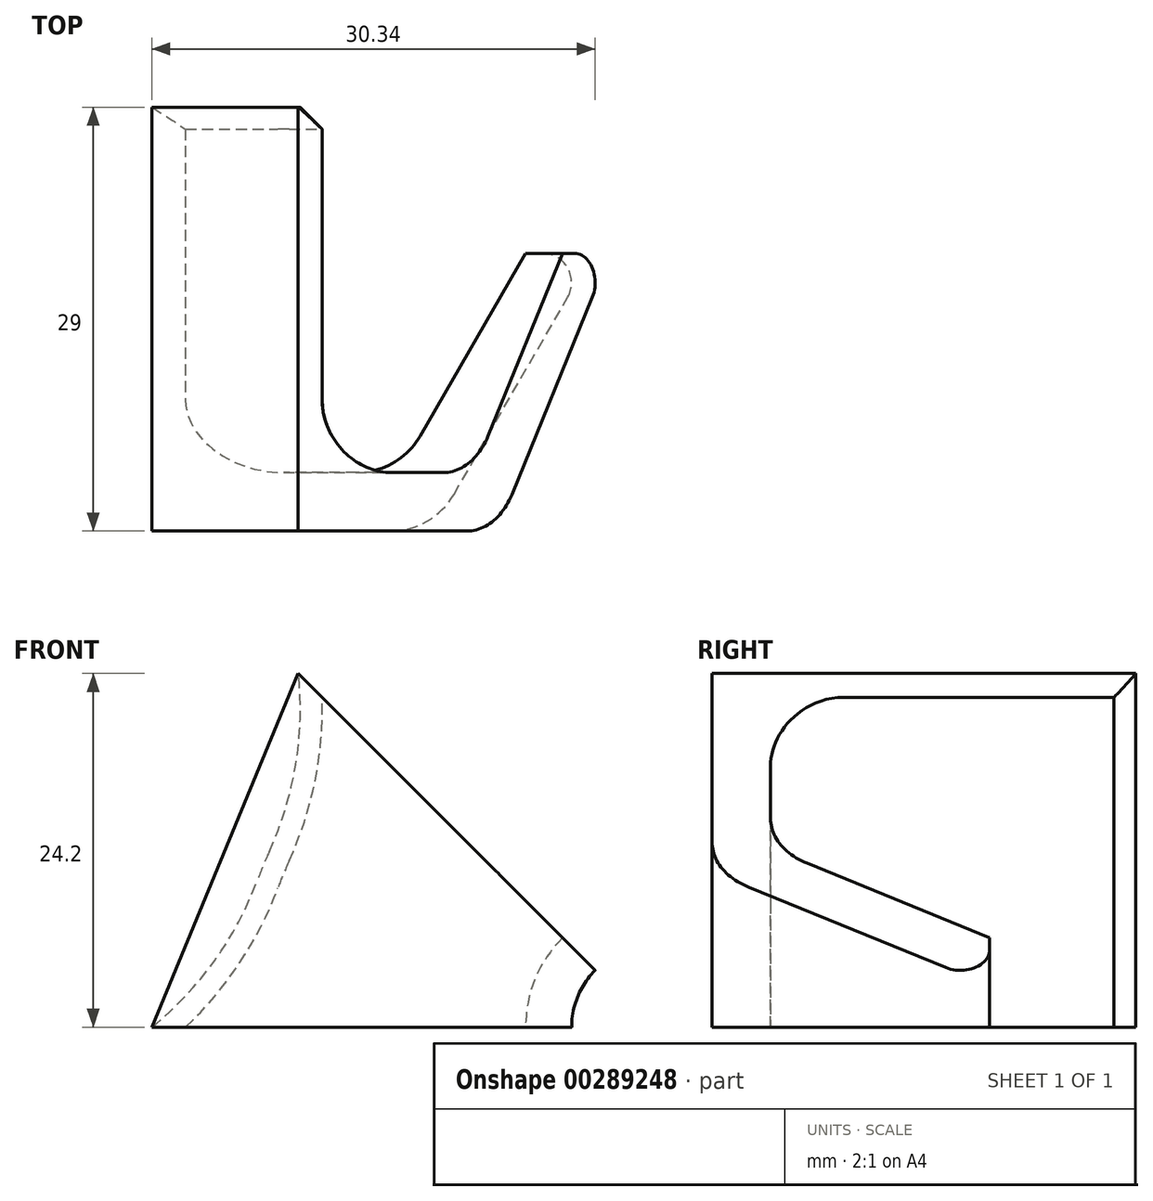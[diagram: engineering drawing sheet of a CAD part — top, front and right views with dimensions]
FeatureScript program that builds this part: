
annotation { "Feature Type Name" : "Feature", "Feature Type Description" : "" }
export const myFeature = defineFeature(function(context is Context, id is Id, definition is map)
    precondition{}
    {
        {
            var Q0;
            Q0=qCreatedBy(makeId("Top.planeOp"),FACE);
            var sketch = newSketch(context, id + "F0", { "sketchPlane" : qUnion([Q0])});
            skLineSegment(sketch, "E0", {"start": v(-8, 25) * mm, "end": v(-8, -4) * mm});
            skLineSegment(sketch, "E1", {"start": v(-8, -4) * mm, "end": v(12.3, -4) * mm});
            skLineSegment(sketch, "E2", {"start": v(12.3, -4) * mm, "end": v(23.28, 15) * mm});
            skLineSegment(sketch, "E3", {"start": v(23.28, 15) * mm, "end": v(18.66, 15) * mm});
            skLineSegment(sketch, "E4", {"start": v(18.66, 15) * mm, "end": v(10, 0) * mm});
            skLineSegment(sketch, "E5", {"start": v(10, 0) * mm, "end": v(0, 0) * mm});
            skLineSegment(sketch, "E6", {"start": v(0, 0) * mm, "end": v(0, 25) * mm});
            skLineSegment(sketch, "E7", {"start": v(0, 25) * mm, "end": v(-8, 25) * mm});
            skLineSegment(sketch, "E8", {"start": v(12.3, -4) * mm, "end": v(27.3, -4) * mm, "construction": true});
            skLineSegment(sketch, "E9", {"start": v(27.3, -4) * mm, "end": v(27.3, 16.04) * mm, "construction": true});
            skSolve(sketch);
        }
        {
            var Q0;
            Q0=makeQuery(id+"F0.imprint","IMPRINT",FACE,{"disambiguationData":[TD([[makeQuery(id+"F0.imprint","IMPRINT",EDGE,{"derivedFrom":sQuery(id+"F0.wireOp",EDGE,"E0")}),1.0]])]});
            var Q1;
            Q1=sQuery(id+"F0.wireOp",EDGE,"E9");
            revolve(context, id + "F1", {"entities" : qUnion([Q0]), "axis" : qUnion([Q1]), "revolveType" : RevolveType.ONE_DIRECTION, "angle" : 45 * degree});
        }
        {
            var Q0;
            Q0=makeQuery(id+"F1.opRevolve","CAP_VERTEX",VERTEX,{"disambiguationData":[OSD([sQuery(id+"F0.wireOp",EDGE,"E0"),sQuery(id+"F0.wireOp",EDGE,"E7")])],"isStart":true});
            var Q1;
            Q1=makeQuery(id+"F1.opRevolve","CAP_VERTEX",VERTEX,{"disambiguationData":[OSD([sQuery(id+"F0.wireOp",EDGE,"E0"),sQuery(id+"F0.wireOp",EDGE,"E1")])],"isStart":true});
            var Q2;
            Q2=makeQuery(id+"F1.opRevolve","CAP_VERTEX",VERTEX,{"disambiguationData":[OSD([sQuery(id+"F0.wireOp",EDGE,"E0"),sQuery(id+"F0.wireOp",EDGE,"E1")])],"isStart":false});
            cPlane(context, id + "F2", {"entities" : qUnion([Q0, Q1, Q2]), "cplaneType" : CPlaneType.THREE_POINT, "offset" : 25 * mm, "width" : 150 * mm, "height" : 150 * mm});
        }
        {
            var Q0;
            Q0=qCreatedBy(id+"F2.planeOp",FACE);
            var sketch = newSketch(context, id + "F3", { "sketchPlane" : qUnion([Q0])});
            skLineSegment(sketch, "E10.bottom", {"start": v(-10.62, 26.87) * mm, "end": v(28.35, 26.87) * mm});
            skLineSegment(sketch, "E10.top", {"start": v(-10.62, -11.64) * mm, "end": v(28.35, -11.64) * mm});
            skLineSegment(sketch, "E10.left", {"start": v(-10.62, 26.87) * mm, "end": v(-10.62, -11.64) * mm});
            skLineSegment(sketch, "E10.right", {"start": v(28.35, 26.87) * mm, "end": v(28.35, -11.64) * mm});
            skSolve(sketch);
        }
        {
            var Q0;
            Q0=makeQuery(id+"F3.imprint","IMPRINT",FACE,{"disambiguationData":[TD([[makeQuery(id+"F3.imprint","IMPRINT",EDGE,{"derivedFrom":sQuery(id+"F3.wireOp",EDGE,"E10.bottom")}),-1.0]])]});
            extrude(context, id + "F4", {"entities" : qUnion([Q0]), "operationType" : NewBodyOperationType.REMOVE, "oppositeDirection" : true, "depth" : 25 * mm, "hasSecondDirection" : true, "secondDirectionOppositeDirection" : false, "secondDirectionDepth" : 1 * mm});
        }
        {
            var Q0;
            Q0=makeQuery(id+"F1.opRevolve","CAP_EDGE",EDGE,{"disambiguationData":[OSD([sQuery(id+"F0.wireOp",EDGE,"E6")])],"isStart":true});
            var Q1;
            Q1=makeQuery(id+"F1.opRevolve","CAP_EDGE",EDGE,{"disambiguationData":[OSD([sQuery(id+"F0.wireOp",EDGE,"E6")])],"isStart":false});
            chamfer(context, id + "F5", {"entities" : qUnion([Q0, Q1]), "width" : 5 * mm, "tangentPropagation" : true});
        }
        {
            var Q0;
            {var subQ0=sQuery(id+"F0.wireOp",EDGE,"E6");Q0=makeQuery(id+"F5.opChamfer","BLEND_EDGE",EDGE,{"blendedFrom":[makeQuery(id+"F1.opRevolve","CAP_EDGE",EDGE,{"disambiguationData":[OSD([subQ0])],"isStart":true}),makeQuery(id+"F1.opRevolve","SWEPT_FACE",FACE,{"disambiguationData":[OSD([subQ0])]})],"blendedInto":[makeQuery(id+"F1.opRevolve","SWEPT_FACE",FACE,{"disambiguationData":[OSD([subQ0])]})]});}
            var Q1;
            {var subQ0=sQuery(id+"F0.wireOp",EDGE,"E6");Q1=makeQuery(id+"F5.opChamfer","BLEND_EDGE",EDGE,{"blendedFrom":[makeQuery(id+"F1.opRevolve","CAP_EDGE",EDGE,{"disambiguationData":[OSD([subQ0])],"isStart":false}),makeQuery(id+"F1.opRevolve","SWEPT_FACE",FACE,{"disambiguationData":[OSD([subQ0])]})],"blendedInto":[makeQuery(id+"F1.opRevolve","SWEPT_FACE",FACE,{"disambiguationData":[OSD([subQ0])]})]});}
            fillet(context, id + "F6", {"entities" : qUnion([Q0, Q1]), "radius" : 25 * mm, "tangentPropagation" : true, "allowEdgeOverflow" : false});
        }
        {
            var Q0;
            Q0=makeQuery(id+"F1.opRevolve","SWEPT_EDGE",EDGE,{"disambiguationData":[OSD([sQuery(id+"F0.wireOp",EDGE,"E4"),sQuery(id+"F0.wireOp",EDGE,"E5")])]});
            var Q1;
            Q1=makeQuery(id+"F1.opRevolve","SWEPT_EDGE",EDGE,{"disambiguationData":[OSD([sQuery(id+"F0.wireOp",EDGE,"E1"),sQuery(id+"F0.wireOp",EDGE,"E2")])]});
            fillet(context, id + "F7", {"entities" : qUnion([Q0, Q1]), "radius" : 5 * mm, "tangentPropagation" : true, "allowEdgeOverflow" : false});
        }
        {
            var Q0;
            Q0=makeQuery(id+"F1.opRevolve","SWEPT_EDGE",EDGE,{"disambiguationData":[OSD([sQuery(id+"F0.wireOp",EDGE,"E6"),sQuery(id+"F0.wireOp",EDGE,"E7")])]});
            var Q1;
            {var subQ0=sQuery(id+"F0.wireOp",EDGE,"E6");Q1=makeQuery(id+"F6.opFillet","BLEND_EDGE",EDGE,{"blendedFrom":[makeQuery(id+"F5.opChamfer","BLEND_EDGE",EDGE,{"blendedFrom":[makeQuery(id+"F1.opRevolve","CAP_EDGE",EDGE,{"disambiguationData":[OSD([subQ0])],"isStart":false}),makeQuery(id+"F1.opRevolve","SWEPT_FACE",FACE,{"disambiguationData":[OSD([subQ0])]})],"blendedInto":[makeQuery(id+"F1.opRevolve","SWEPT_FACE",FACE,{"disambiguationData":[OSD([subQ0])]})]}),makeQuery(id+"F1.opRevolve","SWEPT_FACE",FACE,{"disambiguationData":[OSD([sQuery(id+"F0.wireOp",EDGE,"E7")])]})],"blendedInto":[makeQuery(id+"F1.opRevolve","SWEPT_FACE",FACE,{"disambiguationData":[OSD([sQuery(id+"F0.wireOp",EDGE,"E7")])]})]});}
            var Q2;
            {var subQ0=sQuery(id+"F0.wireOp",EDGE,"E6");Q2=makeQuery(id+"F6.opFillet","BLEND_EDGE",EDGE,{"blendedFrom":[makeQuery(id+"F5.opChamfer","BLEND_EDGE",EDGE,{"blendedFrom":[makeQuery(id+"F1.opRevolve","CAP_EDGE",EDGE,{"disambiguationData":[OSD([subQ0])],"isStart":true}),makeQuery(id+"F1.opRevolve","SWEPT_FACE",FACE,{"disambiguationData":[OSD([subQ0])]})],"blendedInto":[makeQuery(id+"F1.opRevolve","SWEPT_FACE",FACE,{"disambiguationData":[OSD([subQ0])]})]}),makeQuery(id+"F1.opRevolve","SWEPT_FACE",FACE,{"disambiguationData":[OSD([sQuery(id+"F0.wireOp",EDGE,"E7")])]})],"blendedInto":[makeQuery(id+"F1.opRevolve","SWEPT_FACE",FACE,{"disambiguationData":[OSD([sQuery(id+"F0.wireOp",EDGE,"E7")])]})]});}
            chamfer(context, id + "F8", {"entities" : qUnion([Q0, Q1, Q2]), "width" : 1.5 * mm, "tangentPropagation" : true});
        }
        {
            var Q0;
            {var subQ0=sQuery(id+"F0.wireOp",EDGE,"E6");Q0=makeQuery(id+"F6.opFillet","BLEND_EDGE",EDGE,{"blendedFrom":[makeQuery(id+"F5.opChamfer","BLEND_EDGE",EDGE,{"blendedFrom":[makeQuery(id+"F1.opRevolve","CAP_EDGE",EDGE,{"disambiguationData":[OSD([subQ0])],"isStart":false}),makeQuery(id+"F1.opRevolve","SWEPT_FACE",FACE,{"disambiguationData":[OSD([subQ0])]})],"blendedInto":[makeQuery(id+"F1.opRevolve","SWEPT_FACE",FACE,{"disambiguationData":[OSD([subQ0])]})]}),makeQuery(id+"F1.opRevolve","SWEPT_FACE",FACE,{"disambiguationData":[OSD([sQuery(id+"F0.wireOp",EDGE,"E5")])]})],"blendedInto":[makeQuery(id+"F1.opRevolve","SWEPT_FACE",FACE,{"disambiguationData":[OSD([sQuery(id+"F0.wireOp",EDGE,"E5")])]})]});}
            var Q1;
            {var subQ0=sQuery(id+"F0.wireOp",EDGE,"E6");Q1=makeQuery(id+"F6.opFillet","BLEND_EDGE",EDGE,{"blendedFrom":[makeQuery(id+"F5.opChamfer","BLEND_EDGE",EDGE,{"blendedFrom":[makeQuery(id+"F1.opRevolve","CAP_EDGE",EDGE,{"disambiguationData":[OSD([subQ0])],"isStart":true}),makeQuery(id+"F1.opRevolve","SWEPT_FACE",FACE,{"disambiguationData":[OSD([subQ0])]})],"blendedInto":[makeQuery(id+"F1.opRevolve","SWEPT_FACE",FACE,{"disambiguationData":[OSD([subQ0])]})]}),makeQuery(id+"F1.opRevolve","SWEPT_FACE",FACE,{"disambiguationData":[OSD([sQuery(id+"F0.wireOp",EDGE,"E5")])]})],"blendedInto":[makeQuery(id+"F1.opRevolve","SWEPT_FACE",FACE,{"disambiguationData":[OSD([sQuery(id+"F0.wireOp",EDGE,"E5")])]})]});}
            var Q2;
            Q2=makeQuery(id+"F1.opRevolve","SWEPT_EDGE",EDGE,{"disambiguationData":[OSD([sQuery(id+"F0.wireOp",EDGE,"E5"),sQuery(id+"F0.wireOp",EDGE,"E6")])]});
            fillet(context, id + "F9", {"entities" : qUnion([Q0, Q1, Q2]), "radius" : 5 * mm, "tangentPropagation" : true, "allowEdgeOverflow" : false});
        }
        {
            var Q0;
            Q0=makeQuery(id+"F1.opRevolve","SWEPT_EDGE",EDGE,{"disambiguationData":[OSD([sQuery(id+"F0.wireOp",EDGE,"E2"),sQuery(id+"F0.wireOp",EDGE,"E3")])]});
            fillet(context, id + "F10", {"entities" : qUnion([Q0]), "radius" : 2 * mm, "tangentPropagation" : true, "allowEdgeOverflow" : false});
        }
    });
